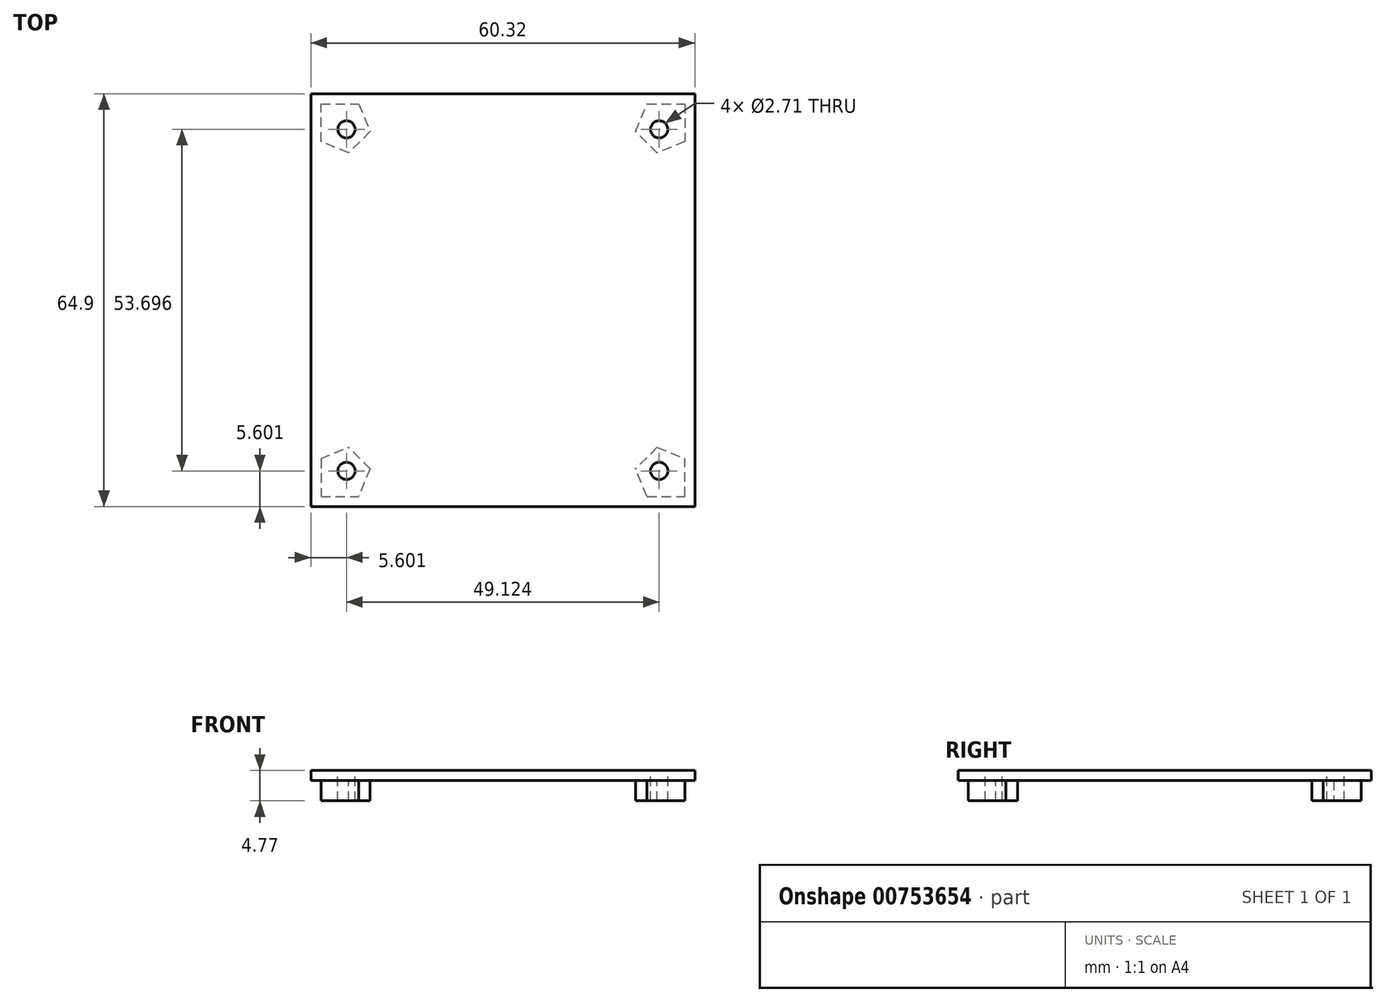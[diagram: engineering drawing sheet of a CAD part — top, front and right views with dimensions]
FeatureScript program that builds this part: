
annotation { "Feature Type Name" : "Feature", "Feature Type Description" : "" }
export const myFeature = defineFeature(function(context is Context, id is Id, definition is map)
    precondition{}
    {
        {
            var Q0;
            Q0=qCreatedBy(makeId("Top.planeOp"),FACE);
            var sketch = newSketch(context, id + "F0", { "sketchPlane" : qUnion([Q0])});
            skLineSegment(sketch, "E0.bottom", {"start": v(0, 0) * mm, "end": v(60.33, 0) * mm});
            skLineSegment(sketch, "E0.top", {"start": v(0, 64.9) * mm, "end": v(60.32, 64.9) * mm});
            skLineSegment(sketch, "E0.left", {"start": v(0, 0) * mm, "end": v(0, 64.9) * mm});
            skLineSegment(sketch, "E0.right", {"start": v(60.33, 0) * mm, "end": v(60.32, 64.9) * mm});
            skSolve(sketch);
        }
        {
            var Q0;
            Q0=makeQuery(id+"F0.imprint","IMPRINT",FACE,{"disambiguationData":[TD([[makeQuery(id+"F0.imprint","IMPRINT",EDGE,{"derivedFrom":sQuery(id+"F0.wireOp",EDGE,"E0.bottom")}),1.0]])]});
            extrude(context, id + "F1", {"entities" : qUnion([Q0]), "depth" : 1.59 * mm, "offsetDistance" : 25.4 * mm});
        }
        {
            var Q0;
            Q0=makeQuery(id+"F1.opExtrude","CAP_FACE",FACE,{"disambiguationData":[OSD([sQuery(id+"F0.wireOp",EDGE,"E0.bottom"),sQuery(id+"F0.wireOp",EDGE,"E0.top"),sQuery(id+"F0.wireOp",EDGE,"E0.left"),sQuery(id+"F0.wireOp",EDGE,"E0.right")])],"isStart":true});
            var sketch = newSketch(context, id + "F2", { "sketchPlane" : qUnion([Q0])});
            skLineSegment(sketch, "E1", {"start": v(58.74, -51.24) * mm, "end": v(46.67, -63.3) * mm});
            skLineSegment(sketch, "E2", {"start": v(46.67, -63.3) * mm, "end": v(58.74, -63.3) * mm});
            skLineSegment(sketch, "E3", {"start": v(58.74, -63.3) * mm, "end": v(58.74, -51.24) * mm});
            skLineSegment(sketch, "E4", {"start": v(46.67, -1.59) * mm, "end": v(58.74, -1.59) * mm});
            skLineSegment(sketch, "E5", {"start": v(58.74, -1.59) * mm, "end": v(58.74, -13.65) * mm});
            skLineSegment(sketch, "E6", {"start": v(58.74, -13.65) * mm, "end": v(46.67, -1.59) * mm});
            skSolve(sketch);
        }
        {
            var Q0;
            Q0 = qSketchRegion(id + "F2", true);
            extrude(context, id + "F3", {"entities" : qUnion([Q0]), "operationType" : NewBodyOperationType.ADD, "depth" : 3.17 * mm, "offsetDistance" : 25.4 * mm});
        }
        {
            var Q0;
            Q0=makeQuery(id+"F1.opExtrude","CAP_FACE",FACE,{"disambiguationData":[OSD([sQuery(id+"F0.wireOp",EDGE,"E0.bottom"),sQuery(id+"F0.wireOp",EDGE,"E0.top"),sQuery(id+"F0.wireOp",EDGE,"E0.left"),sQuery(id+"F0.wireOp",EDGE,"E0.right")])],"isStart":true});
            var sketch = newSketch(context, id + "F4", { "sketchPlane" : qUnion([Q0])});
            skLineSegment(sketch, "E7", {"start": v(1.59, -1.59) * mm, "end": v(13.65, -1.59) * mm});
            skLineSegment(sketch, "E8", {"start": v(13.65, -1.59) * mm, "end": v(1.59, -13.65) * mm});
            skLineSegment(sketch, "E9", {"start": v(1.59, -13.65) * mm, "end": v(1.59, -1.59) * mm});
            skLineSegment(sketch, "E10", {"start": v(1.59, -63.3) * mm, "end": v(13.65, -63.3) * mm});
            skLineSegment(sketch, "E11", {"start": v(13.65, -63.3) * mm, "end": v(1.59, -51.24) * mm});
            skLineSegment(sketch, "E12", {"start": v(1.59, -51.24) * mm, "end": v(1.59, -63.3) * mm});
            skSolve(sketch);
        }
        {
            var Q0;
            Q0 = qSketchRegion(id + "F4", true);
            extrude(context, id + "F5", {"entities" : qUnion([Q0]), "operationType" : NewBodyOperationType.ADD, "depth" : 3.17 * mm, "offsetDistance" : 25.4 * mm});
        }
        {
            var Q0;
            Q0=makeQuery(id+"F1.opExtrude","CAP_FACE",FACE,{"disambiguationData":[OSD([sQuery(id+"F0.wireOp",EDGE,"E0.bottom"),sQuery(id+"F0.wireOp",EDGE,"E0.top"),sQuery(id+"F0.wireOp",EDGE,"E0.left"),sQuery(id+"F0.wireOp",EDGE,"E0.right")])],"isStart":false});
            var sketch = newSketch(context, id + "F6", { "sketchPlane" : qUnion([Q0])});
            skPoint(sketch, "E13", {"position": v(54.72, 5.6) * mm});
            skPoint(sketch, "E14", {"position": v(54.72, 59.3) * mm});
            skPoint(sketch, "E15", {"position": v(5.6, 5.6) * mm});
            skPoint(sketch, "E16", {"position": v(5.6, 59.3) * mm});
            skSolve(sketch);
        }
        {
            var Q0;
            Q0=sQuery(id+"F6.wireOp",VERTEX,"E14");
            var Q1;
            Q1=sQuery(id+"F6.wireOp",VERTEX,"E13");
            var Q2;
            Q2=sQuery(id+"F6.wireOp",VERTEX,"E15");
            var Q3;
            Q3=sQuery(id+"F6.wireOp",VERTEX,"E16");
            var Q4;
            Q4=makeQuery(id+"F1.opExtrude","SWEPT_BODY",BODY,{"disambiguationData":[OSD([sQuery(id+"F0.wireOp",EDGE,"E0.bottom"),sQuery(id+"F0.wireOp",EDGE,"E0.top"),sQuery(id+"F0.wireOp",EDGE,"E0.left"),sQuery(id+"F0.wireOp",EDGE,"E0.right")])]});
            hole(context, id + "F7", {"style" : HoleStyle.SIMPLE, "endStyle" : HoleEndStyle.THROUGH, "standardTappedOrClearance" : lookupTablePath({ "standard" : "ANSI", "engagement" : "75%", "pitch" : "32 tpi", "size" : "#6", "type" : "Tapped" }), "standardBlindInLast" : lookupTablePath({ "standard" : "ANSI", "engagement" : "75%", "pitch" : "32 tpi", "size" : "#6", "type" : "Tapped" }), "holeDiameter" : 2.7 * mm, "majorDiameter" : 3.5 * mm, "showTappedDepth" : true, "isTappedThrough" : true, "tappedDepth" : 5.56 * mm, "tapClearance" : 3, "locations" : qUnion([Q0, Q1, Q2, Q3]), "scope" : qUnion([Q4])});
        }
        {
            var Q0;
            Q0=makeQuery(id+"F3.opExtrude","SWEPT_EDGE",EDGE,{"disambiguationData":[OSD([sQuery(id+"F2.wireOp",EDGE,"E4"),sQuery(id+"F2.wireOp",EDGE,"E6")])]});
            var Q1;
            Q1=makeQuery(id+"F3.opExtrude","SWEPT_EDGE",EDGE,{"disambiguationData":[OSD([sQuery(id+"F2.wireOp",EDGE,"E5"),sQuery(id+"F2.wireOp",EDGE,"E6")])]});
            var Q2;
            Q2=makeQuery(id+"F3.opExtrude","SWEPT_EDGE",EDGE,{"disambiguationData":[OSD([sQuery(id+"F2.wireOp",EDGE,"E1"),sQuery(id+"F2.wireOp",EDGE,"E3")])]});
            var Q3;
            Q3=makeQuery(id+"F3.opExtrude","SWEPT_EDGE",EDGE,{"disambiguationData":[OSD([sQuery(id+"F2.wireOp",EDGE,"E1"),sQuery(id+"F2.wireOp",EDGE,"E2")])]});
            var Q4;
            Q4=makeQuery(id+"F5.opExtrude","SWEPT_EDGE",EDGE,{"disambiguationData":[OSD([sQuery(id+"F4.wireOp",EDGE,"E7"),sQuery(id+"F4.wireOp",EDGE,"E8")])]});
            var Q5;
            Q5=makeQuery(id+"F5.opExtrude","SWEPT_EDGE",EDGE,{"disambiguationData":[OSD([sQuery(id+"F4.wireOp",EDGE,"E8"),sQuery(id+"F4.wireOp",EDGE,"E9")])]});
            var Q6;
            Q6=makeQuery(id+"F5.opExtrude","SWEPT_EDGE",EDGE,{"disambiguationData":[OSD([sQuery(id+"F4.wireOp",EDGE,"E11"),sQuery(id+"F4.wireOp",EDGE,"E12")])]});
            var Q7;
            Q7=makeQuery(id+"F5.opExtrude","SWEPT_EDGE",EDGE,{"disambiguationData":[OSD([sQuery(id+"F4.wireOp",EDGE,"E10"),sQuery(id+"F4.wireOp",EDGE,"E11")])]});
            chamfer(context, id + "F8", {"entities" : qUnion([Q0, Q1, Q2, Q3, Q4, Q5, Q6, Q7]), "width" : 2.54 * mm, "tangentPropagation" : true});
        }
    });
